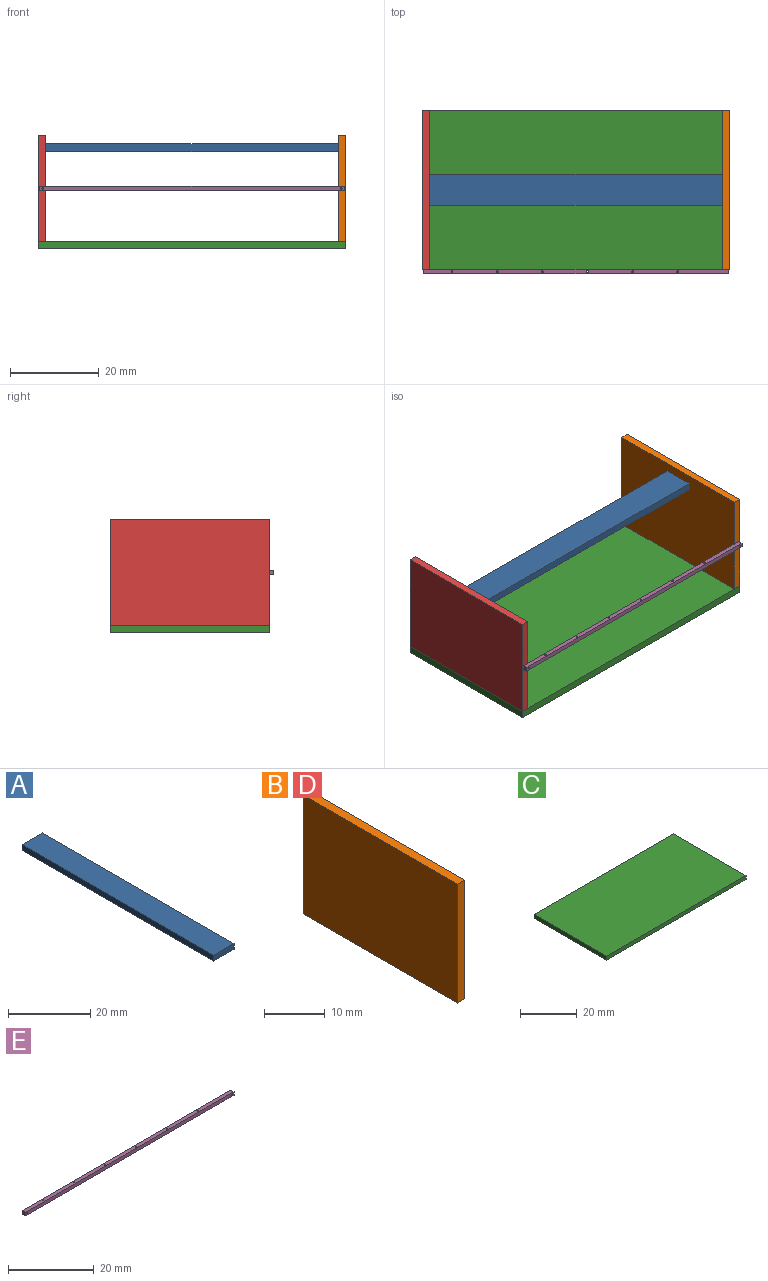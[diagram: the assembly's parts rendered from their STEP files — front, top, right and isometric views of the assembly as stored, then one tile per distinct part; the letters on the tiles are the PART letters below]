
ASSEMBLY  parts=5 mates=4
PART A: 6 faces, bbox 7x66x1.7 mm
  f0: plane 66x1.7mm, normal (-1,0,0), area 112.2mm2, adj f1,f3,f4,f5
  f1: plane 7x1.7mm, normal (0,-1,0), area 11.9mm2, adj f0,f2,f4,f5
  f2: plane 66x1.7mm, normal (1,0,0), area 112.2mm2, adj f1,f3,f4,f5
  f3: plane 7x1.7mm, normal (0,1,0), area 11.9mm2, adj f0,f2,f4,f5
  f4: plane 66x7mm, normal (0,0,1), area 462mm2, adj f0,f1,f2,f3
  f5: plane 66x7mm, normal (0,0,-1), area 462mm2, adj f0,f1,f2,f3
PART B: 6 faces, bbox 1.7x36x24 mm
  f0: plane 24x1.7mm, normal (0,-1,0), area 40.8mm2, adj f1,f3,f4,f5
  f1: plane 36x1.7mm, normal (0,0,-1), area 61.2mm2, adj f0,f2,f4,f5
  f2: plane 24x1.7mm, normal (0,1,0), area 40.8mm2, adj f1,f3,f4,f5
  f3: plane 36x1.7mm, normal (0,0,1), area 61.2mm2, adj f0,f2,f4,f5
  f4: plane 36x24mm, normal (1,0,0), area 864mm2, adj f0,f1,f2,f3
  f5: plane 36x24mm, normal (-1,0,0), area 864mm2, adj f0,f1,f2,f3
PART C: 6 faces, bbox 69.4x36x1.7 mm
  f0: plane 36x1.7mm, normal (-1,0,0), area 61.2mm2, adj f1,f3,f4,f5
  f1: plane 69.4x1.7mm, normal (0,-1,0), area 118mm2, adj f0,f2,f4,f5
  f2: plane 36x1.7mm, normal (1,0,0), area 61.2mm2, adj f1,f3,f4,f5
  f3: plane 69.4x1.7mm, normal (0,1,0), area 118mm2, adj f0,f2,f4,f5
  f4: plane 69.4x36mm, normal (0,0,1), area 2498.4mm2, adj f0,f1,f2,f3
  f5: plane 69.4x36mm, normal (0,0,-1), area 2498.4mm2, adj f0,f1,f2,f3
PART D: same geometry as B
PART E: 14 faces, bbox 68.8x1x1 mm
  f0: plane 68.8x1mm, normal (0,0,-1), area 68mm2, adj f1,f3,f4,f5,f8,f9,f10,f11
  f1: plane 1x1mm, normal (1,0,0), area 1mm2, adj f0,f2,f4,f5
  f2: plane 68.8x1mm, normal (0,0,1), area 68mm2, adj f1,f3,f4,f5,f8,f9,f10,f11
  f3: plane 1x1mm, normal (-1,0,0), area 1mm2, adj f0,f2,f4,f5
  f4: plane 68.8x1mm, normal (0,-1,0), area 68.5mm2, adj f0,f1,f2,f3,f6,f7
  f5: plane 68.8x1mm, normal (0,1,0), area 68.5mm2, adj f0,f1,f2,f3,f6,f7
  f6: cylinder r=0.2mm len=1mm, axis (0,-1,0), area 1.3mm2, adj f4,f5
  f7: cylinder r=0.2mm len=1mm, axis (0,-1,0), area 1.3mm2, adj f4,f5
  f8: cylinder r=0.2mm len=1mm, axis (0,0,1), area 1.3mm2, adj f0,f2
  f9: cylinder r=0.2mm len=1mm, axis (0,0,1), area 1.3mm2, adj f0,f2
  f10: cylinder r=0.2mm len=1mm, axis (0,0,1), area 1.3mm2, adj f0,f2
  f11: cylinder r=0.2mm len=1mm, axis (0,0,1), area 1.3mm2, adj f0,f2
  f12: cylinder r=0.2mm len=1mm, axis (0,0,1), area 1.3mm2, adj f0,f2
  f13: cylinder r=0.2mm len=1mm, axis (0,0,1), area 1.3mm2, adj f0,f2
PLACE A rot(axis=(0.71,0.71,0),180deg) t=(-45.53,1.17,14.87)mm
PLACE B t=(20.47,-13.33,-7.13)mm
PLACE C t=(-12.23,4.67,-8.83)mm
PLACE D t=(-47.23,-13.33,-7.13)mm
PLACE E t=(21.87,-13.33,4.37)mm
MATE fastened D.f1 <-> C.f4  axis (0,0,-1) through (-47.23,4.67,-7.13)mm
MATE fastened E.f5 <-> D.f0  axis (0,1,0) through (-46.93,-13.33,4.87)mm
MATE fastened A.f1 <-> D.f4  axis (-1,0,0) through (-45.53,4.67,13.17)mm
MATE fastened B.f1 <-> C.f4  axis (0,0,-1) through (22.17,4.67,-7.13)mm
